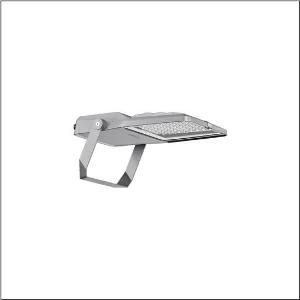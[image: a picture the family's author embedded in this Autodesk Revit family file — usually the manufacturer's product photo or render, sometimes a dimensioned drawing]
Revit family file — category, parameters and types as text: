
# Revit family: floodlight_fl_21_iq_mini___pl61_5xa7772b3c1a_b78d
name_source: partatom
category: Lighting Fixtures
units: mm (PartAtom-declared; Revit-internal decimal feet)

## family parameters
Cut with Voids When Loaded = No
Host = Face
Light Source = No
Part Type = Normal
Room Calculation Point = No
Round Connector Dimension = Use Diameter
Shared = No

## types (1)
- --- (1 x LED, 5270 lm, 45.5 W, 3000K)
    Apparent Load = 46 VA
    CIE Flux Codes = 33 65 98 100 100
    Color Rendering = 80
    Color Temperature = 3000K
    Default Elevation = 1800 mm
    Description = Floodlight FL 21 iQ mini, floodlight, primary light control with lens, of PMMA, primary optical cover: protective disc, of toughened safety glass, transparent, light distribution: PL61, light emission: direct distribution, installation type: surface-mounted, LED, High Power LED, rated luminous flux: 5.270lm, luminous efficacy: 116lm/W, light colour: 830, colour temperature: 3000K, control: Street-Remote, Auto-Match, Temp-Guard, Night-Set, Smart-Wire, Desk-Remote (wireless, voltage-free reading and setting of iQ features in the workshop via application-optimized NFC function/RFID function), optimised constant luminous flux control (CLO 2.0), with terminal, 6-pole, mains connection: 220..240V, AC, 50/60Hz, start of lifetime: 46W, end of service life: 48W, reduction: 21W, luminaire housing, of diecast aluminium, powder-coated, Siteco® metallic grey (DB 702S), corrosivity category C5 mid according to DIN EN ISO 12944, sealing non-destructively replaceable, mounting bracket, of steel, galvanised, powder-coated, Siteco® metallic grey (DB 702S), protection rating (complete): IP66, insulation class (complete): insulation class II (safety insulation), certification: CE, ENEC, VDE, protection symbol: D, impact resistance: IK08, permissible operating ambient temperature: -40..+40°C, permissible operating ambient temperature for outdoor applications: -40..+50°C, standard: DIN EN 12944, LABS conformity tested according to VDMA 24364:2018-05, packaging unit: 1 piece

Light Distribution: PL61
    Height = 70 mm
    Lamp = 1 x LED
    Lamp Light Flux = 5270 lm
    Lamp Power = 45.5 W
    Lamp count = 1
    Length = 485 mm
    Luminous efficacy = 116 lm/W
    Manufacturer = Siteco
    ModVariant = No
    Model = 5XA7772B3C1A
    Number of Poles = 1
    OnlyDefault = Yes
    Power Factor = 1
    Product Name = Floodlight FL 21 iQ mini | PL61
    Product group = floodlight | pylon annexe
    ProductGroupID = 6200
    Protection Class = Protection class II
    Protection Degree = IP 66
    RLX_Detail_Level = 1
    RLX_Emergency_Light_Flux = 0 lm
    RLX_Emergency_Type = 0
    RLX_Emergency_Type_DB = No
    RlxData = <blob elided: 96405 chars, md5=c78bce3c>
    Socket = socket
    Standby Power = 0 W
    System Light Flux = 5270 lm
    System Power = 46 W
    Type Comments = factory setting: luminous flux: 100 % | dim-lin: 254 | 463 mA
    Type Image = l_1006845.jpg
    URL = http://relux.com
    VarID = @adj_124475
    Voltage = 0 V
    Weight = 0.00 kg
    Width = 337 mm

## geometry (parser evidence)
native form markers: Blend x4, Sweep x11
no freeform markers — native parametric forms only
